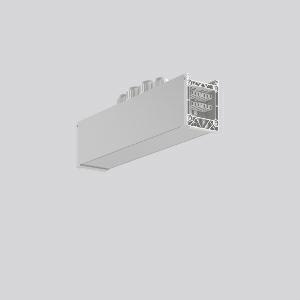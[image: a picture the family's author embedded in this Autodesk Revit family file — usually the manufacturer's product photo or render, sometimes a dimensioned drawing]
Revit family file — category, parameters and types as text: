
# Revit family: linedo_mitteleinspeisung_7pol_b_b_982698_000_4_184a
name_source: partatom
category: Lighting Fixtures
units: mm (PartAtom-declared; Revit-internal decimal feet)

## family parameters
Cut with Voids When Loaded = No
Host = Face
Light Source = No
Part Type = Normal
Room Calculation Point = No
Round Connector Dimension = Use Diameter
Shared = No

## types (1)
- LINEDO_Mitteleinspeisung_7pol_B_B
    Apparent Load = 0 VA
    Default Elevation = 1800 mm
    Description = Series: LINEDO
Middle power feed, 7-pole, connection socket / socket. Housing: extruded aluminium profile, anodised. Cover made of plastic, surface like housing. LINEDO plug system, plastic, light grey. 4 cable glands (2 x M20 and 2 x M25). Cable glands on top. Easy connection for rigid or flexible wires.
Colour: anodised aluminium
Length: 312 mm
Width: 58 mm
Height: 76 mm
Weight: 751 g
    Height = 76 mm
    Lamp = 0 x
    Length = 312 mm
    Luminous efficacy = 0 lm/W
    Manufacturer = RZB
    ModVariant = No
    Model = 982698.000.4
    Mounting Place = Ceiling
    Mounting Type = Surface mounted, Pendant
    Number of Poles = 1
    OnlyDefault = Yes
    Power Factor = 1
    Product Name = LINEDO_Mitteleinspeisung_7pol_B_B
    Product group = Surface mounted continuous line luminaire system
    ProductGroupID = 310
    Protection Class = Protection class I
    Protection Degree = IP 54
    RLX_Detail_Level = 1
    RLX_Emergency_Light_Flux = 0 lm
    RLX_Emergency_Type = 0
    RLX_Emergency_Type_DB = No
    RlxData = <blob elided: 22017 chars, md5=261e0250>
    Standby Power = 0 W
    System Light Flux = 0 lm
    System Power = 0 W
    Type Comments = Product without accessories
    Type Image = 982698.000.1.jpg
    URL = http://relux.com
    VarID = ---
    Voltage = 0 V
    Weight = 0.00 kg
    Width = 58 mm

## geometry (parser evidence)
native form markers: Blend x4, Sweep x11
no freeform markers — native parametric forms only
